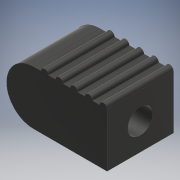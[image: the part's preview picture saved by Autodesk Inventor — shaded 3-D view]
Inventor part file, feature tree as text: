
AUTODESK INVENTOR PART (.ipt)
format: ipt  version: 2019 (Build 230136000, 136)  size: 133,120 bytes
history: native  units: mm
features: extrude x3, sketch x3, pattern_linear x1
ambient origin geometry x8: Origin, YZ Plane, XZ Plane, XY Plane, X Axis, Y Axis, Z Axis, Center Point
bodies: Solid1 (feature_tree)
feature tree (7):
  extrude  "Extrusion1"  Depth=7.3mm
  extrude  "Extrusion2"  Depth=9.0mm
  pattern_linear  "Rectangular Pattern1"  Count1=5 Spacing1=2.0mm
  extrude  "Extrusion3"  Depth=4.0mm
  sketch  "Sketch1"  dims[d0=10.0mm d1=7.3mm]
  sketch  "Sketch2"  dims[d2=9.0mm d3=0.0mm d4=1.0mm]
  sketch  "Sketch3"  dims[d5=9.0mm d6=0.0mm d7=50.0mm d9=2.0mm d10=3.4mm d11=4.0mm d12=0.0mm]
